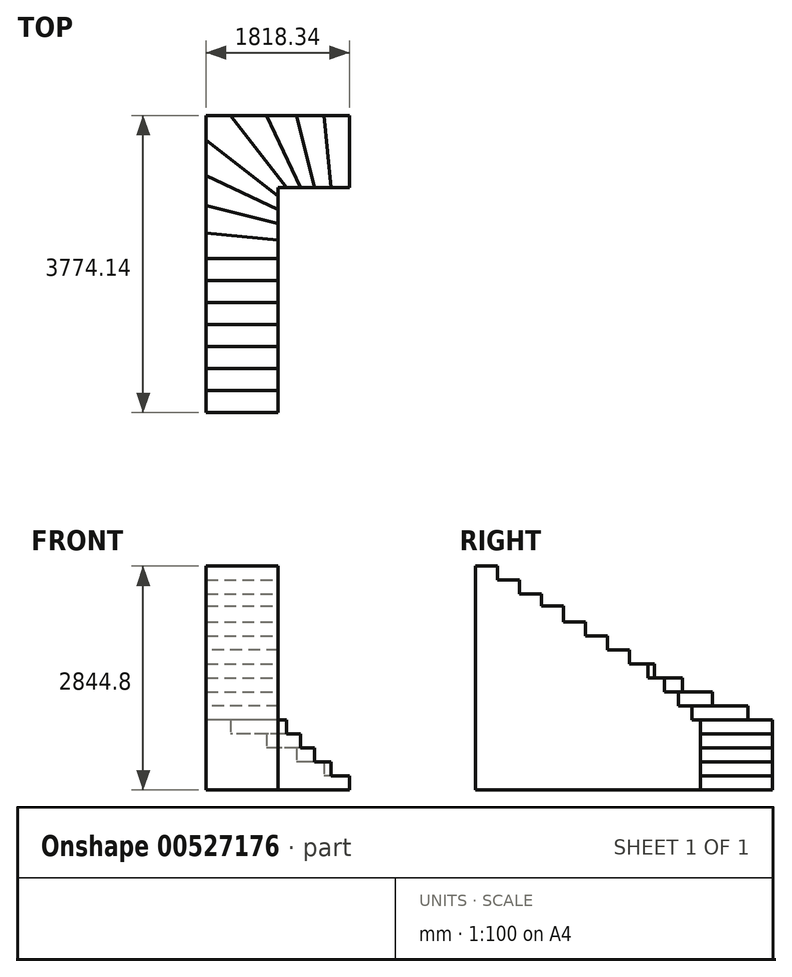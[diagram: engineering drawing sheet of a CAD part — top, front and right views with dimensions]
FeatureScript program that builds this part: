
annotation { "Feature Type Name" : "Feature", "Feature Type Description" : "" }
export const myFeature = defineFeature(function(context is Context, id is Id, definition is map)
    precondition{}
    {
        {
            var Q0;
            Q0=qCreatedBy(makeId("Top.planeOp"),FACE);
            var sketch = newSketch(context, id + "F0", { "sketchPlane" : qUnion([Q0])});
            skArc(sketch, "E0", {"start": v(0, 457.2) * mm, "mid": v(-323.29, 323.29) * mm, "end": v(-457.2, 0) * mm});
            skLineSegment(sketch, "E1", {"start": v(0, 457.2) * mm, "end": v(1462.74, 457.2) * mm});
            skLineSegment(sketch, "E2", {"start": v(-457.2, 0) * mm, "end": v(-457.2, -3139.14) * mm});
            skPoint(sketch, "E3", {"position": v(-406.61, 209.04) * mm});
            skPoint(sketch, "E4", {"position": v(-209.04, 406.61) * mm});
            skLineSegment(sketch, "E5", {"start": v(0, 0) * mm, "end": v(1462.74, 0) * mm});
            skLineSegment(sketch, "E6", {"start": v(1462.74, 0) * mm, "end": v(1462.74, 914.4) * mm});
            skLineSegment(sketch, "E7", {"start": v(1462.74, 914.4) * mm, "end": v(-914.4, 914.4) * mm});
            skLineSegment(sketch, "E8", {"start": v(-914.4, 914.4) * mm, "end": v(-914.4, -3139.14) * mm});
            skLineSegment(sketch, "E9", {"start": v(-914.4, -3139.14) * mm, "end": v(0, -3139.14) * mm});
            skLineSegment(sketch, "E10", {"start": v(0, -3139.14) * mm, "end": v(0, 0) * mm});
            skLineSegment(sketch, "E11", {"start": v(-914.4, 914.4) * mm, "end": v(0, 0) * mm});
            skLineSegment(sketch, "E12", {"start": v(-806.64, 914.4) * mm, "end": v(107.76, 0) * mm, "construction": true});
            skLineSegment(sketch, "E13", {"start": v(-914.4, 806.64) * mm, "end": v(0, -107.76) * mm, "construction": true});
            skPoint(sketch, "E14", {"position": v(65.74, 457.2) * mm});
            skPoint(sketch, "E15", {"position": v(-457.2, -65.74) * mm});
            skPoint(sketch, "E16", {"position": v(345.14, 457.2) * mm});
            skPoint(sketch, "E17", {"position": v(624.54, 457.2) * mm});
            skPoint(sketch, "E18", {"position": v(903.94, 457.2) * mm});
            skLineSegment(sketch, "E19", {"start": v(0, 0) * mm, "end": v(903.94, -903.94) * mm, "construction": true});
            skLineSegment(sketch, "E20", {"start": v(107.76, 0) * mm, "end": v(-604.69, 914.4) * mm});
            skLineSegment(sketch, "E21", {"start": v(0, -107.76) * mm, "end": v(-914.4, 604.69) * mm});
            skLineSegment(sketch, "E22", {"start": v(107.76, 0) * mm, "end": v(487.93, -487.93) * mm, "construction": true});
            skLineSegment(sketch, "E23", {"start": v(487.93, -487.93) * mm, "end": v(993.99, -443.5) * mm, "construction": true});
            skPoint(sketch, "E24", {"position": v(538.54, -483.5) * mm});
            skPoint(sketch, "E25", {"position": v(639.75, -474.6) * mm});
            skPoint(sketch, "E26", {"position": v(791.56, -461.28) * mm});
            skLineSegment(sketch, "E27", {"start": v(993.99, -443.5) * mm, "end": v(903.94, -903.94) * mm, "construction": true});
            skLineSegment(sketch, "E28", {"start": v(791.56, -461.28) * mm, "end": v(737.54, -737.54) * mm, "construction": true});
            skLineSegment(sketch, "E29", {"start": v(639.75, -474.6) * mm, "end": v(612.73, -612.73) * mm, "construction": true});
            skLineSegment(sketch, "E30", {"start": v(538.54, -483.5) * mm, "end": v(529.53, -529.53) * mm, "construction": true});
            skPoint(sketch, "E31", {"position": v(-457.2, -345.14) * mm});
            skPoint(sketch, "E32", {"position": v(-457.2, -624.54) * mm});
            skPoint(sketch, "E33", {"position": v(-457.2, -903.94) * mm});
            skPoint(sketch, "E34", {"position": v(-457.2, -1183.34) * mm});
            skLineSegment(sketch, "E35.trimOffspring", {"start": v(280.64, 0) * mm, "end": v(-149.16, 914.4) * mm});
            skLineSegment(sketch, "E36", {"start": v(667.78, 0) * mm, "end": v(581.3, 914.4) * mm});
            skLineSegment(sketch, "E37", {"start": v(459.49, 0) * mm, "end": v(230.79, 914.4) * mm});
            skLineSegment(sketch, "E38", {"start": v(280.64, 0) * mm, "end": v(529.53, -529.53) * mm, "construction": true});
            skLineSegment(sketch, "E39", {"start": v(612.73, -612.73) * mm, "end": v(459.49, 0) * mm, "construction": true});
            skLineSegment(sketch, "E40", {"start": v(737.54, -737.54) * mm, "end": v(667.78, 0) * mm, "construction": true});
            skLineSegment(sketch, "E41", {"start": v(903.94, 914.4) * mm, "end": v(903.94, 0) * mm});
            skLineSegment(sketch, "E42", {"start": v(903.94, -903.94) * mm, "end": v(903.94, 0) * mm, "construction": true});
            skPoint(sketch, "E43", {"position": v(-457.2, -1462.74) * mm});
            skPoint(sketch, "E44", {"position": v(-457.2, -1742.14) * mm});
            skPoint(sketch, "E45", {"position": v(-457.2, -2021.54) * mm});
            skPoint(sketch, "E46", {"position": v(-457.2, -2300.94) * mm});
            skPoint(sketch, "E47", {"position": v(-457.2, -2580.34) * mm});
            skPoint(sketch, "E48", {"position": v(-457.2, -2859.74) * mm});
            skPoint(sketch, "E49", {"position": v(1183.34, 457.2) * mm});
            skLineSegment(sketch, "E50", {"start": v(1183.34, 914.4) * mm, "end": v(1183.34, 0) * mm});
            skLineSegment(sketch, "E51", {"start": v(-914.4, 149.16) * mm, "end": v(0, -280.64) * mm});
            skLineSegment(sketch, "E52", {"start": v(0, -280.64) * mm, "end": v(529.53, -529.53) * mm, "construction": true});
            skLineSegment(sketch, "E53", {"start": v(-914.4, -230.79) * mm, "end": v(0, -459.49) * mm});
            skLineSegment(sketch, "E54", {"start": v(0, -459.49) * mm, "end": v(612.73, -612.73) * mm, "construction": true});
            skLineSegment(sketch, "E55", {"start": v(-914.4, -581.3) * mm, "end": v(0, -667.78) * mm});
            skLineSegment(sketch, "E56", {"start": v(0, -667.78) * mm, "end": v(737.54, -737.54) * mm, "construction": true});
            skLineSegment(sketch, "E57", {"start": v(903.94, -903.94) * mm, "end": v(0, -903.94) * mm, "construction": true});
            skLineSegment(sketch, "E58", {"start": v(0, -903.94) * mm, "end": v(-914.4, -903.94) * mm});
            skLineSegment(sketch, "E59", {"start": v(-914.4, -1183.34) * mm, "end": v(0, -1183.34) * mm});
            skLineSegment(sketch, "E60", {"start": v(-914.4, -1462.74) * mm, "end": v(0, -1462.74) * mm});
            skLineSegment(sketch, "E61", {"start": v(-914.4, -1742.14) * mm, "end": v(0, -1742.14) * mm});
            skLineSegment(sketch, "E62", {"start": v(-914.4, -2021.54) * mm, "end": v(0, -2021.54) * mm});
            skLineSegment(sketch, "E63", {"start": v(-914.4, -2300.94) * mm, "end": v(0, -2300.94) * mm});
            skLineSegment(sketch, "E64", {"start": v(-914.4, -2580.34) * mm, "end": v(0, -2580.34) * mm});
            skLineSegment(sketch, "E65", {"start": v(-914.4, -2859.74) * mm, "end": v(0, -2859.74) * mm});
            skSolve(sketch);
        }
        {
            var Q0;
            {var subQ0=sQuery(id+"F0.wireOp",EDGE,"E36");var subQ1=sQuery(id+"F0.wireOp",EDGE,"E1");var subQ2=makeQuery(id+"F0.imprint","INTERSECT",VERTEX,{"derivedFrom":[subQ1,subQ0]});Q0=makeQuery(id+"F0.imprint","IMPRINT",FACE,{"disambiguationData":[TD([[makeQuery(id+"F0.imprint","IMPRINT",EDGE,{"disambiguationData":[TD([[subQ2,-1.0]])],"derivedFrom":subQ1}),1.0]])]});}
            var Q1;
            {var subQ0=sQuery(id+"F0.wireOp",EDGE,"E36");var subQ1=sQuery(id+"F0.wireOp",EDGE,"E1");var subQ2=makeQuery(id+"F0.imprint","INTERSECT",VERTEX,{"derivedFrom":[subQ1,subQ0]});Q1=makeQuery(id+"F0.imprint","IMPRINT",FACE,{"disambiguationData":[TD([[makeQuery(id+"F0.imprint","IMPRINT",EDGE,{"disambiguationData":[TD([[subQ2,-1.0]])],"derivedFrom":subQ1}),-1.0]])]});}
            extrude(context, id + "F1", {"entities" : qUnion([Q0, Q1]), "depth" : 177.8 * mm, "offsetDistance" : 25.4 * mm});
        }
        {
            var Q0;
            {var subQ0=sQuery(id+"F0.wireOp",EDGE,"E37");var subQ1=sQuery(id+"F0.wireOp",EDGE,"E1");var subQ2=makeQuery(id+"F0.imprint","INTERSECT",VERTEX,{"derivedFrom":[subQ1,subQ0]});Q0=makeQuery(id+"F0.imprint","IMPRINT",FACE,{"disambiguationData":[TD([[makeQuery(id+"F0.imprint","IMPRINT",EDGE,{"disambiguationData":[TD([[subQ2,-1.0]])],"derivedFrom":subQ1}),1.0]])]});}
            var Q1;
            {var subQ0=sQuery(id+"F0.wireOp",EDGE,"E37");var subQ1=sQuery(id+"F0.wireOp",EDGE,"E1");var subQ2=makeQuery(id+"F0.imprint","INTERSECT",VERTEX,{"derivedFrom":[subQ1,subQ0]});Q1=makeQuery(id+"F0.imprint","IMPRINT",FACE,{"disambiguationData":[TD([[makeQuery(id+"F0.imprint","IMPRINT",EDGE,{"disambiguationData":[TD([[subQ2,-1.0]])],"derivedFrom":subQ1}),-1.0]])]});}
            extrude(context, id + "F2", {"entities" : qUnion([Q0, Q1]), "operationType" : NewBodyOperationType.ADD, "depth" : 355.6 * mm, "offsetDistance" : 25.4 * mm});
        }
        {
            var Q0;
            {var subQ0=sQuery(id+"F0.wireOp",EDGE,"E35.trimOffspring");var subQ1=sQuery(id+"F0.wireOp",EDGE,"E1");var subQ2=makeQuery(id+"F0.imprint","INTERSECT",VERTEX,{"derivedFrom":[subQ1,subQ0]});Q0=makeQuery(id+"F0.imprint","IMPRINT",FACE,{"disambiguationData":[TD([[makeQuery(id+"F0.imprint","IMPRINT",EDGE,{"disambiguationData":[TD([[subQ2,-1.0]])],"derivedFrom":subQ1}),1.0]])]});}
            var Q1;
            {var subQ0=sQuery(id+"F0.wireOp",EDGE,"E35.trimOffspring");var subQ1=sQuery(id+"F0.wireOp",EDGE,"E1");var subQ2=makeQuery(id+"F0.imprint","INTERSECT",VERTEX,{"derivedFrom":[subQ1,subQ0]});Q1=makeQuery(id+"F0.imprint","IMPRINT",FACE,{"disambiguationData":[TD([[makeQuery(id+"F0.imprint","IMPRINT",EDGE,{"disambiguationData":[TD([[subQ2,-1.0]])],"derivedFrom":subQ1}),-1.0]])]});}
            extrude(context, id + "F3", {"entities" : qUnion([Q0, Q1]), "operationType" : NewBodyOperationType.ADD, "depth" : 533.4 * mm, "offsetDistance" : 25.4 * mm});
        }
        {
            var Q0;
            {var subQ5=sQuery(id+"F0.wireOp",EDGE,"E0");var subQ7=sQuery(id+"F0.wireOp",EDGE,"E1");var subQ8=makeQuery(id+"F0.imprint","INTERSECT",VERTEX,{"derivedFrom":[subQ5,subQ7]});Q0=makeQuery(id+"F0.imprint","IMPRINT",FACE,{"disambiguationData":[TD([[makeQuery(id+"F0.imprint","IMPRINT",EDGE,{"disambiguationData":[TD([[subQ8,-1.0]])],"derivedFrom":subQ5}),-1.0]])]});}
            var Q1;
            {var subQ3=sQuery(id+"F0.wireOp",EDGE,"E0");var subQ7=sQuery(id+"F0.wireOp",EDGE,"E1");var subQ8=makeQuery(id+"F0.imprint","INTERSECT",VERTEX,{"derivedFrom":[subQ3,subQ7]});Q1=makeQuery(id+"F0.imprint","IMPRINT",FACE,{"disambiguationData":[TD([[makeQuery(id+"F0.imprint","IMPRINT",EDGE,{"disambiguationData":[TD([[subQ8,-1.0]])],"derivedFrom":subQ3}),1.0]])]});}
            extrude(context, id + "F4", {"entities" : qUnion([Q0, Q1]), "operationType" : NewBodyOperationType.ADD, "depth" : 711.2 * mm, "offsetDistance" : 25.4 * mm});
        }
        {
            var Q0;
            {var subQ0=sQuery(id+"F0.wireOp",EDGE,"E20");var subQ1=sQuery(id+"F0.wireOp",EDGE,"E0");var subQ2=makeQuery(id+"F0.imprint","INTERSECT",VERTEX,{"derivedFrom":[subQ1,subQ0]});Q0=makeQuery(id+"F0.imprint","IMPRINT",FACE,{"disambiguationData":[TD([[makeQuery(id+"F0.imprint","IMPRINT",EDGE,{"disambiguationData":[TD([[subQ2,-1.0]])],"derivedFrom":subQ1}),-1.0]])]});}
            var Q1;
            {var subQ0=sQuery(id+"F0.wireOp",EDGE,"E20");var subQ1=sQuery(id+"F0.wireOp",EDGE,"E0");var subQ2=makeQuery(id+"F0.imprint","INTERSECT",VERTEX,{"derivedFrom":[subQ1,subQ0]});Q1=makeQuery(id+"F0.imprint","IMPRINT",FACE,{"disambiguationData":[TD([[makeQuery(id+"F0.imprint","IMPRINT",EDGE,{"disambiguationData":[TD([[subQ2,-1.0]])],"derivedFrom":subQ1}),1.0]])]});}
            var Q2;
            {var subQ0=sQuery(id+"F0.wireOp",EDGE,"E11");var subQ1=sQuery(id+"F0.wireOp",EDGE,"E0");var subQ2=makeQuery(id+"F0.imprint","INTERSECT",VERTEX,{"derivedFrom":[subQ1,subQ0]});Q2=makeQuery(id+"F0.imprint","IMPRINT",FACE,{"disambiguationData":[TD([[makeQuery(id+"F0.imprint","IMPRINT",EDGE,{"disambiguationData":[TD([[subQ2,-1.0]])],"derivedFrom":subQ1}),-1.0]])]});}
            var Q3;
            {var subQ0=sQuery(id+"F0.wireOp",EDGE,"E11");var subQ1=sQuery(id+"F0.wireOp",EDGE,"E0");var subQ2=makeQuery(id+"F0.imprint","INTERSECT",VERTEX,{"derivedFrom":[subQ1,subQ0]});Q3=makeQuery(id+"F0.imprint","IMPRINT",FACE,{"disambiguationData":[TD([[makeQuery(id+"F0.imprint","IMPRINT",EDGE,{"disambiguationData":[TD([[subQ2,-1.0]])],"derivedFrom":subQ1}),1.0]])]});}
            extrude(context, id + "F5", {"entities" : qUnion([Q0, Q1, Q2, Q3]), "operationType" : NewBodyOperationType.ADD, "depth" : 889 * mm, "offsetDistance" : 25.4 * mm});
        }
        {
            var Q0;
            {var subQ3=sQuery(id+"F0.wireOp",EDGE,"E0");var subQ7=sQuery(id+"F0.wireOp",EDGE,"E2");var subQ9=makeQuery(id+"F0.imprint","INTERSECT",VERTEX,{"derivedFrom":[subQ3,subQ7]});Q0=makeQuery(id+"F0.imprint","IMPRINT",FACE,{"disambiguationData":[TD([[makeQuery(id+"F0.imprint","IMPRINT",EDGE,{"disambiguationData":[TD([[subQ9,1.0]])],"derivedFrom":subQ3}),-1.0]])]});}
            var Q1;
            {var subQ5=sQuery(id+"F0.wireOp",EDGE,"E0");var subQ7=sQuery(id+"F0.wireOp",EDGE,"E2");var subQ8=makeQuery(id+"F0.imprint","INTERSECT",VERTEX,{"derivedFrom":[subQ5,subQ7]});Q1=makeQuery(id+"F0.imprint","IMPRINT",FACE,{"disambiguationData":[TD([[makeQuery(id+"F0.imprint","IMPRINT",EDGE,{"disambiguationData":[TD([[subQ8,1.0]])],"derivedFrom":subQ5}),1.0]])]});}
            extrude(context, id + "F6", {"entities" : qUnion([Q0, Q1]), "operationType" : NewBodyOperationType.ADD, "depth" : 1066.8 * mm, "offsetDistance" : 25.4 * mm});
        }
        {
            var Q0;
            {var subQ0=sQuery(id+"F0.wireOp",EDGE,"E51");var subQ1=sQuery(id+"F0.wireOp",EDGE,"E2");var subQ2=makeQuery(id+"F0.imprint","INTERSECT",VERTEX,{"derivedFrom":[subQ1,subQ0]});Q0=makeQuery(id+"F0.imprint","IMPRINT",FACE,{"disambiguationData":[TD([[makeQuery(id+"F0.imprint","IMPRINT",EDGE,{"disambiguationData":[TD([[subQ2,-1.0]])],"derivedFrom":subQ1}),-1.0]])]});}
            var Q1;
            {var subQ0=sQuery(id+"F0.wireOp",EDGE,"E51");var subQ1=sQuery(id+"F0.wireOp",EDGE,"E2");var subQ2=makeQuery(id+"F0.imprint","INTERSECT",VERTEX,{"derivedFrom":[subQ1,subQ0]});Q1=makeQuery(id+"F0.imprint","IMPRINT",FACE,{"disambiguationData":[TD([[makeQuery(id+"F0.imprint","IMPRINT",EDGE,{"disambiguationData":[TD([[subQ2,-1.0]])],"derivedFrom":subQ1}),1.0]])]});}
            extrude(context, id + "F7", {"entities" : qUnion([Q0, Q1]), "operationType" : NewBodyOperationType.ADD, "depth" : 1244.6 * mm, "offsetDistance" : 25.4 * mm});
        }
        {
            var Q0;
            {var subQ0=sQuery(id+"F0.wireOp",EDGE,"E53");var subQ1=sQuery(id+"F0.wireOp",EDGE,"E2");var subQ2=makeQuery(id+"F0.imprint","INTERSECT",VERTEX,{"derivedFrom":[subQ1,subQ0]});Q0=makeQuery(id+"F0.imprint","IMPRINT",FACE,{"disambiguationData":[TD([[makeQuery(id+"F0.imprint","IMPRINT",EDGE,{"disambiguationData":[TD([[subQ2,-1.0]])],"derivedFrom":subQ1}),-1.0]])]});}
            var Q1;
            {var subQ0=sQuery(id+"F0.wireOp",EDGE,"E53");var subQ1=sQuery(id+"F0.wireOp",EDGE,"E2");var subQ2=makeQuery(id+"F0.imprint","INTERSECT",VERTEX,{"derivedFrom":[subQ1,subQ0]});Q1=makeQuery(id+"F0.imprint","IMPRINT",FACE,{"disambiguationData":[TD([[makeQuery(id+"F0.imprint","IMPRINT",EDGE,{"disambiguationData":[TD([[subQ2,-1.0]])],"derivedFrom":subQ1}),1.0]])]});}
            extrude(context, id + "F8", {"entities" : qUnion([Q0, Q1]), "operationType" : NewBodyOperationType.ADD, "depth" : 1422.4 * mm, "offsetDistance" : 25.4 * mm});
        }
        {
            var Q0;
            {var subQ0=sQuery(id+"F0.wireOp",EDGE,"E55");var subQ1=sQuery(id+"F0.wireOp",EDGE,"E2");var subQ2=makeQuery(id+"F0.imprint","INTERSECT",VERTEX,{"derivedFrom":[subQ1,subQ0]});Q0=makeQuery(id+"F0.imprint","IMPRINT",FACE,{"disambiguationData":[TD([[makeQuery(id+"F0.imprint","IMPRINT",EDGE,{"disambiguationData":[TD([[subQ2,-1.0]])],"derivedFrom":subQ1}),-1.0]])]});}
            var Q1;
            {var subQ0=sQuery(id+"F0.wireOp",EDGE,"E55");var subQ1=sQuery(id+"F0.wireOp",EDGE,"E2");var subQ2=makeQuery(id+"F0.imprint","INTERSECT",VERTEX,{"derivedFrom":[subQ1,subQ0]});Q1=makeQuery(id+"F0.imprint","IMPRINT",FACE,{"disambiguationData":[TD([[makeQuery(id+"F0.imprint","IMPRINT",EDGE,{"disambiguationData":[TD([[subQ2,-1.0]])],"derivedFrom":subQ1}),1.0]])]});}
            extrude(context, id + "F9", {"entities" : qUnion([Q0, Q1]), "operationType" : NewBodyOperationType.ADD, "depth" : 1600.2 * mm, "offsetDistance" : 25.4 * mm});
        }
        {
            var Q0;
            {var subQ0=sQuery(id+"F0.wireOp",EDGE,"E58");var subQ1=sQuery(id+"F0.wireOp",EDGE,"E2");var subQ2=makeQuery(id+"F0.imprint","INTERSECT",VERTEX,{"derivedFrom":[subQ1,subQ0]});Q0=makeQuery(id+"F0.imprint","IMPRINT",FACE,{"disambiguationData":[TD([[makeQuery(id+"F0.imprint","IMPRINT",EDGE,{"disambiguationData":[TD([[subQ2,-1.0]])],"derivedFrom":subQ1}),-1.0]])]});}
            var Q1;
            {var subQ0=sQuery(id+"F0.wireOp",EDGE,"E58");var subQ1=sQuery(id+"F0.wireOp",EDGE,"E2");var subQ2=makeQuery(id+"F0.imprint","INTERSECT",VERTEX,{"derivedFrom":[subQ1,subQ0]});Q1=makeQuery(id+"F0.imprint","IMPRINT",FACE,{"disambiguationData":[TD([[makeQuery(id+"F0.imprint","IMPRINT",EDGE,{"disambiguationData":[TD([[subQ2,-1.0]])],"derivedFrom":subQ1}),1.0]])]});}
            extrude(context, id + "F10", {"entities" : qUnion([Q0, Q1]), "operationType" : NewBodyOperationType.ADD, "depth" : 1778 * mm, "offsetDistance" : 25.4 * mm});
        }
        {
            var Q0;
            {var subQ0=sQuery(id+"F0.wireOp",EDGE,"E59");var subQ1=sQuery(id+"F0.wireOp",EDGE,"E2");var subQ2=makeQuery(id+"F0.imprint","INTERSECT",VERTEX,{"derivedFrom":[subQ1,subQ0]});Q0=makeQuery(id+"F0.imprint","IMPRINT",FACE,{"disambiguationData":[TD([[makeQuery(id+"F0.imprint","IMPRINT",EDGE,{"disambiguationData":[TD([[subQ2,-1.0]])],"derivedFrom":subQ1}),-1.0]])]});}
            var Q1;
            {var subQ0=sQuery(id+"F0.wireOp",EDGE,"E59");var subQ1=sQuery(id+"F0.wireOp",EDGE,"E2");var subQ2=makeQuery(id+"F0.imprint","INTERSECT",VERTEX,{"derivedFrom":[subQ1,subQ0]});Q1=makeQuery(id+"F0.imprint","IMPRINT",FACE,{"disambiguationData":[TD([[makeQuery(id+"F0.imprint","IMPRINT",EDGE,{"disambiguationData":[TD([[subQ2,-1.0]])],"derivedFrom":subQ1}),1.0]])]});}
            extrude(context, id + "F11", {"entities" : qUnion([Q0, Q1]), "operationType" : NewBodyOperationType.ADD, "depth" : 1955.8 * mm, "offsetDistance" : 25.4 * mm});
        }
        {
            var Q0;
            {var subQ0=sQuery(id+"F0.wireOp",EDGE,"E60");var subQ1=sQuery(id+"F0.wireOp",EDGE,"E2");var subQ2=makeQuery(id+"F0.imprint","INTERSECT",VERTEX,{"derivedFrom":[subQ1,subQ0]});Q0=makeQuery(id+"F0.imprint","IMPRINT",FACE,{"disambiguationData":[TD([[makeQuery(id+"F0.imprint","IMPRINT",EDGE,{"disambiguationData":[TD([[subQ2,-1.0]])],"derivedFrom":subQ1}),-1.0]])]});}
            var Q1;
            {var subQ0=sQuery(id+"F0.wireOp",EDGE,"E60");var subQ1=sQuery(id+"F0.wireOp",EDGE,"E2");var subQ2=makeQuery(id+"F0.imprint","INTERSECT",VERTEX,{"derivedFrom":[subQ1,subQ0]});Q1=makeQuery(id+"F0.imprint","IMPRINT",FACE,{"disambiguationData":[TD([[makeQuery(id+"F0.imprint","IMPRINT",EDGE,{"disambiguationData":[TD([[subQ2,-1.0]])],"derivedFrom":subQ1}),1.0]])]});}
            extrude(context, id + "F12", {"entities" : qUnion([Q0, Q1]), "operationType" : NewBodyOperationType.ADD, "depth" : 2133.6 * mm, "offsetDistance" : 25.4 * mm});
        }
        {
            var Q0;
            {var subQ0=sQuery(id+"F0.wireOp",EDGE,"E61");var subQ1=sQuery(id+"F0.wireOp",EDGE,"E2");var subQ2=makeQuery(id+"F0.imprint","INTERSECT",VERTEX,{"derivedFrom":[subQ1,subQ0]});Q0=makeQuery(id+"F0.imprint","IMPRINT",FACE,{"disambiguationData":[TD([[makeQuery(id+"F0.imprint","IMPRINT",EDGE,{"disambiguationData":[TD([[subQ2,-1.0]])],"derivedFrom":subQ1}),-1.0]])]});}
            var Q1;
            {var subQ0=sQuery(id+"F0.wireOp",EDGE,"E61");var subQ1=sQuery(id+"F0.wireOp",EDGE,"E2");var subQ2=makeQuery(id+"F0.imprint","INTERSECT",VERTEX,{"derivedFrom":[subQ1,subQ0]});Q1=makeQuery(id+"F0.imprint","IMPRINT",FACE,{"disambiguationData":[TD([[makeQuery(id+"F0.imprint","IMPRINT",EDGE,{"disambiguationData":[TD([[subQ2,-1.0]])],"derivedFrom":subQ1}),1.0]])]});}
            extrude(context, id + "F13", {"entities" : qUnion([Q0, Q1]), "operationType" : NewBodyOperationType.ADD, "depth" : 2336.8 * mm, "offsetDistance" : 25.4 * mm});
        }
        {
            var Q0;
            {var subQ0=sQuery(id+"F0.wireOp",EDGE,"E62");var subQ1=sQuery(id+"F0.wireOp",EDGE,"E2");var subQ2=makeQuery(id+"F0.imprint","INTERSECT",VERTEX,{"derivedFrom":[subQ1,subQ0]});Q0=makeQuery(id+"F0.imprint","IMPRINT",FACE,{"disambiguationData":[TD([[makeQuery(id+"F0.imprint","IMPRINT",EDGE,{"disambiguationData":[TD([[subQ2,-1.0]])],"derivedFrom":subQ1}),-1.0]])]});}
            var Q1;
            {var subQ0=sQuery(id+"F0.wireOp",EDGE,"E62");var subQ1=sQuery(id+"F0.wireOp",EDGE,"E2");var subQ2=makeQuery(id+"F0.imprint","INTERSECT",VERTEX,{"derivedFrom":[subQ1,subQ0]});Q1=makeQuery(id+"F0.imprint","IMPRINT",FACE,{"disambiguationData":[TD([[makeQuery(id+"F0.imprint","IMPRINT",EDGE,{"disambiguationData":[TD([[subQ2,-1.0]])],"derivedFrom":subQ1}),1.0]])]});}
            extrude(context, id + "F14", {"entities" : qUnion([Q0, Q1]), "operationType" : NewBodyOperationType.ADD, "depth" : 2489.2 * mm, "offsetDistance" : 25.4 * mm});
        }
        {
            var Q0;
            {var subQ0=sQuery(id+"F0.wireOp",EDGE,"E63");var subQ1=sQuery(id+"F0.wireOp",EDGE,"E2");var subQ2=makeQuery(id+"F0.imprint","INTERSECT",VERTEX,{"derivedFrom":[subQ1,subQ0]});Q0=makeQuery(id+"F0.imprint","IMPRINT",FACE,{"disambiguationData":[TD([[makeQuery(id+"F0.imprint","IMPRINT",EDGE,{"disambiguationData":[TD([[subQ2,-1.0]])],"derivedFrom":subQ1}),-1.0]])]});}
            var Q1;
            {var subQ0=sQuery(id+"F0.wireOp",EDGE,"E63");var subQ1=sQuery(id+"F0.wireOp",EDGE,"E2");var subQ2=makeQuery(id+"F0.imprint","INTERSECT",VERTEX,{"derivedFrom":[subQ1,subQ0]});Q1=makeQuery(id+"F0.imprint","IMPRINT",FACE,{"disambiguationData":[TD([[makeQuery(id+"F0.imprint","IMPRINT",EDGE,{"disambiguationData":[TD([[subQ2,-1.0]])],"derivedFrom":subQ1}),1.0]])]});}
            extrude(context, id + "F15", {"entities" : qUnion([Q0, Q1]), "operationType" : NewBodyOperationType.ADD, "depth" : 2667 * mm, "offsetDistance" : 25.4 * mm});
        }
        {
            var Q0;
            {var subQ0=sQuery(id+"F0.wireOp",EDGE,"E64");var subQ1=sQuery(id+"F0.wireOp",EDGE,"E2");var subQ2=makeQuery(id+"F0.imprint","INTERSECT",VERTEX,{"derivedFrom":[subQ1,subQ0]});Q0=makeQuery(id+"F0.imprint","IMPRINT",FACE,{"disambiguationData":[TD([[makeQuery(id+"F0.imprint","IMPRINT",EDGE,{"disambiguationData":[TD([[subQ2,-1.0]])],"derivedFrom":subQ1}),-1.0]])]});}
            var Q1;
            {var subQ0=sQuery(id+"F0.wireOp",EDGE,"E64");var subQ1=sQuery(id+"F0.wireOp",EDGE,"E2");var subQ2=makeQuery(id+"F0.imprint","INTERSECT",VERTEX,{"derivedFrom":[subQ1,subQ0]});Q1=makeQuery(id+"F0.imprint","IMPRINT",FACE,{"disambiguationData":[TD([[makeQuery(id+"F0.imprint","IMPRINT",EDGE,{"disambiguationData":[TD([[subQ2,-1.0]])],"derivedFrom":subQ1}),1.0]])]});}
            extrude(context, id + "F16", {"entities" : qUnion([Q0, Q1]), "operationType" : NewBodyOperationType.ADD, "depth" : 2844.8 * mm, "offsetDistance" : 25.4 * mm});
        }
    });
